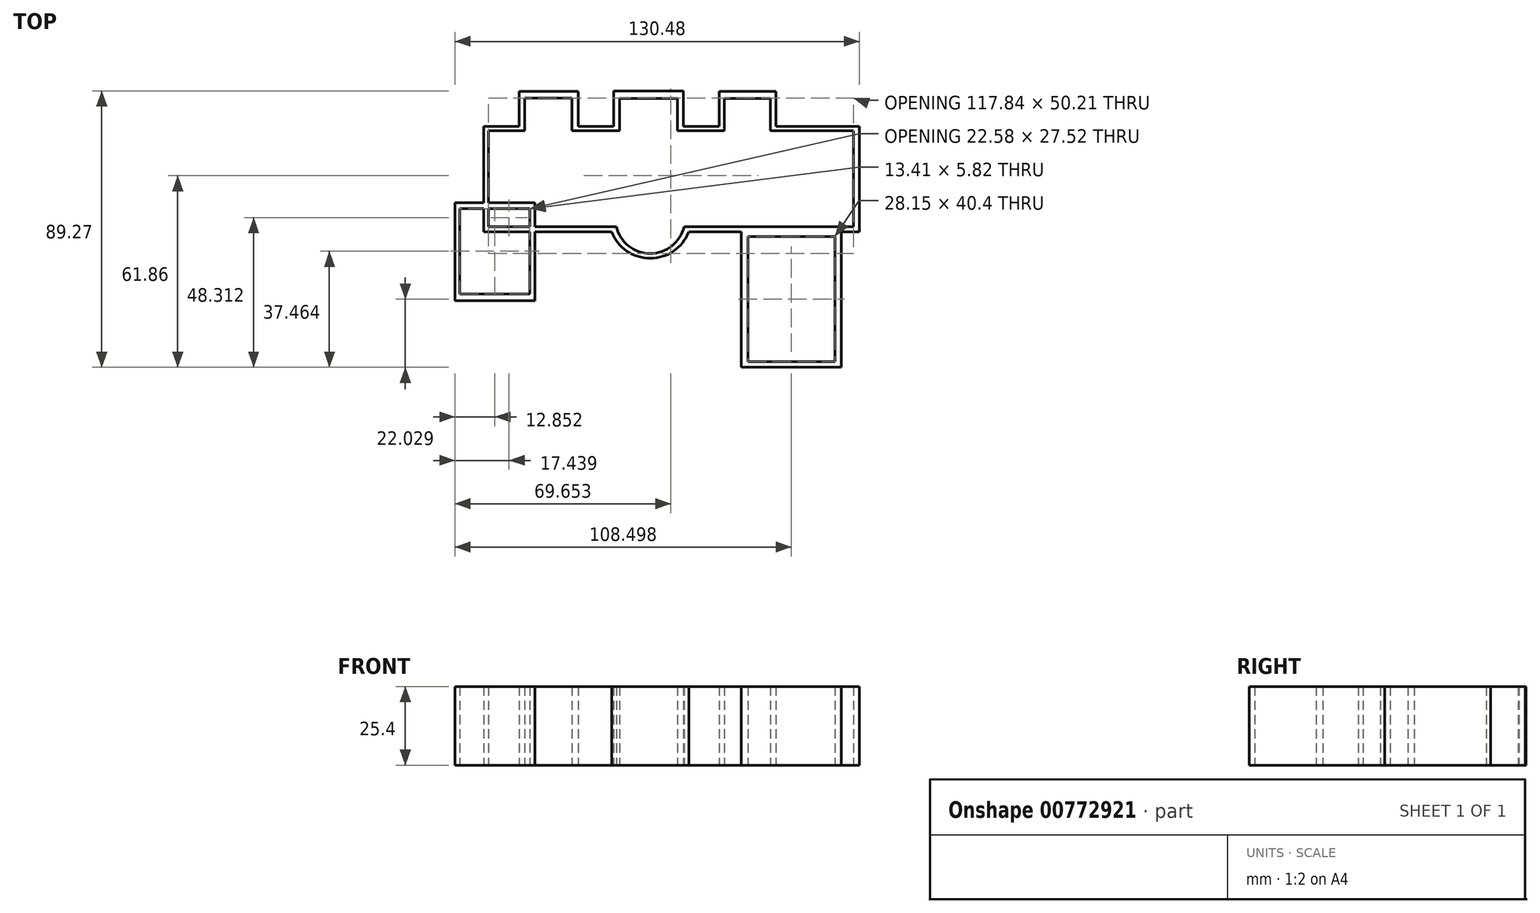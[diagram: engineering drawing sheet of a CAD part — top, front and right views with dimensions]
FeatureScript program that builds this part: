
annotation { "Feature Type Name" : "Feature", "Feature Type Description" : "" }
export const myFeature = defineFeature(function(context is Context, id is Id, definition is map)
    precondition{}
    {
        {
            var Q0;
            Q0=qCreatedBy(makeId("Top.planeOp"),FACE);
            var sketch = newSketch(context, id + "F0", { "sketchPlane" : qUnion([Q0])});
            skLineSegment(sketch, "E0.bottom", {"start": v(-53.74, 34.1) * mm, "end": v(67.5, 34.1) * mm});
            skLineSegment(sketch, "E0.top", {"start": v(-53.74, 0) * mm, "end": v(67.5, 0) * mm});
            skLineSegment(sketch, "E0.left", {"start": v(-53.74, 34.1) * mm, "end": v(-53.74, 0) * mm});
            skLineSegment(sketch, "E0.right", {"start": v(67.5, 34.1) * mm, "end": v(67.5, 0) * mm});
            skLineSegment(sketch, "E1.bottom", {"start": v(29.35, 0) * mm, "end": v(61.62, 0) * mm});
            skLineSegment(sketch, "E1.top", {"start": v(29.35, -43.74) * mm, "end": v(61.62, -43.74) * mm});
            skLineSegment(sketch, "E1.left", {"start": v(29.35, 0) * mm, "end": v(29.35, -43.74) * mm});
            skLineSegment(sketch, "E1.right", {"start": v(61.62, 0) * mm, "end": v(61.62, -43.74) * mm});
            skLineSegment(sketch, "E2.bottom", {"start": v(-62.98, 9.47) * mm, "end": v(-37.22, 9.47) * mm});
            skLineSegment(sketch, "E2.top", {"start": v(-62.98, -22.18) * mm, "end": v(-37.22, -22.18) * mm});
            skLineSegment(sketch, "E2.left", {"start": v(-62.98, 9.47) * mm, "end": v(-62.98, -22.18) * mm});
            skLineSegment(sketch, "E2.right", {"start": v(-37.22, 9.47) * mm, "end": v(-37.22, -22.18) * mm});
            skLineSegment(sketch, "E3.bottom", {"start": v(-42.26, 34.1) * mm, "end": v(-23.22, 34.1) * mm});
            skLineSegment(sketch, "E3.top", {"start": v(-42.26, 45.3) * mm, "end": v(-23.22, 45.3) * mm});
            skLineSegment(sketch, "E3.left", {"start": v(-42.26, 34.1) * mm, "end": v(-42.26, 45.3) * mm});
            skLineSegment(sketch, "E3.right", {"start": v(-23.22, 34.1) * mm, "end": v(-23.22, 45.3) * mm});
            skLineSegment(sketch, "E4.top", {"start": v(22.28, 45.3) * mm, "end": v(40.48, 45.3) * mm});
            skLineSegment(sketch, "E4.left", {"start": v(22.28, 34.1) * mm, "end": v(22.28, 45.3) * mm});
            skLineSegment(sketch, "E4.right", {"start": v(40.48, 34.1) * mm, "end": v(40.48, 45.3) * mm});
            skLineSegment(sketch, "E5.top", {"start": v(-11.74, 45.53) * mm, "end": v(10.63, 45.53) * mm});
            skLineSegment(sketch, "E5.left", {"start": v(-11.74, 34.1) * mm, "end": v(-11.74, 45.53) * mm});
            skLineSegment(sketch, "E5.right", {"start": v(10.63, 34.1) * mm, "end": v(10.63, 45.53) * mm});
            skLineSegment(sketch, "E6.bottom", {"start": v(-61.42, 7.48) * mm, "end": v(-38.84, 7.48) * mm});
            skLineSegment(sketch, "E6.top", {"start": v(-61.42, -20.04) * mm, "end": v(-38.84, -20.04) * mm});
            skLineSegment(sketch, "E6.left", {"start": v(-61.42, 7.48) * mm, "end": v(-61.42, -20.04) * mm});
            skLineSegment(sketch, "E6.right", {"start": v(-38.84, 7.48) * mm, "end": v(-38.84, -20.04) * mm});
            skLineSegment(sketch, "E7.bottom", {"start": v(-52.24, 32.7) * mm, "end": v(65.6, 32.7) * mm});
            skLineSegment(sketch, "E7.top", {"start": v(-52.24, 1.66) * mm, "end": v(65.6, 1.66) * mm});
            skLineSegment(sketch, "E7.left", {"start": v(-52.24, 32.7) * mm, "end": v(-52.24, 1.66) * mm});
            skLineSegment(sketch, "E7.right", {"start": v(65.6, 32.7) * mm, "end": v(65.6, 1.66) * mm});
            skLineSegment(sketch, "E8.bottom", {"start": v(31.44, -1.51) * mm, "end": v(59.6, -1.51) * mm});
            skLineSegment(sketch, "E8.top", {"start": v(31.44, -41.9) * mm, "end": v(59.6, -41.9) * mm});
            skLineSegment(sketch, "E8.left", {"start": v(31.44, -1.51) * mm, "end": v(31.44, -41.9) * mm});
            skLineSegment(sketch, "E8.right", {"start": v(59.6, -1.51) * mm, "end": v(59.6, -41.9) * mm});
            skLineSegment(sketch, "E9.bottom", {"start": v(-40.56, 43.23) * mm, "end": v(-25.23, 43.23) * mm});
            skLineSegment(sketch, "E9.top", {"start": v(-40.56, 34.1) * mm, "end": v(-25.23, 34.1) * mm});
            skLineSegment(sketch, "E9.left", {"start": v(-40.56, 43.23) * mm, "end": v(-40.56, 34.1) * mm});
            skLineSegment(sketch, "E9.right", {"start": v(-25.23, 43.23) * mm, "end": v(-25.23, 34.1) * mm});
            skLineSegment(sketch, "E10.bottom", {"start": v(-9.9, 43) * mm, "end": v(8.78, 43) * mm});
            skLineSegment(sketch, "E10.top", {"start": v(-9.9, 34.1) * mm, "end": v(8.78, 34.1) * mm});
            skLineSegment(sketch, "E10.left", {"start": v(-9.9, 43) * mm, "end": v(-9.9, 34.1) * mm});
            skLineSegment(sketch, "E10.right", {"start": v(8.78, 43) * mm, "end": v(8.78, 34.1) * mm});
            skLineSegment(sketch, "E11.bottom", {"start": v(23.9, 43) * mm, "end": v(38.76, 43) * mm});
            skLineSegment(sketch, "E11.top", {"start": v(23.9, 34.1) * mm, "end": v(38.76, 34.1) * mm});
            skLineSegment(sketch, "E11.left", {"start": v(23.9, 43) * mm, "end": v(23.9, 34.1) * mm});
            skLineSegment(sketch, "E11.right", {"start": v(38.76, 43) * mm, "end": v(38.76, 34.1) * mm});
            skArc(sketch, "E12", {"start": v(-12.45, 0) * mm, "mid": v(-0.02, -8.53) * mm, "end": v(12.4, 0) * mm});
            skArc(sketch, "E13", {"start": v(-10.96, 1.66) * mm, "mid": v(-0.02, -6.99) * mm, "end": v(10.91, 1.66) * mm});
            skLineSegment(sketch, "E14", {"start": v(31.44, -1.51) * mm, "end": v(31.44, 1.66) * mm});
            skLineSegment(sketch, "E15", {"start": v(-40.56, 34.1) * mm, "end": v(-40.56, 32.7) * mm});
            skLineSegment(sketch, "E16", {"start": v(-25.23, 34.1) * mm, "end": v(-25.23, 32.7) * mm});
            skLineSegment(sketch, "E17", {"start": v(-9.9, 34.1) * mm, "end": v(-9.9, 32.7) * mm});
            skLineSegment(sketch, "E18", {"start": v(8.78, 34.1) * mm, "end": v(8.78, 32.7) * mm});
            skLineSegment(sketch, "E19", {"start": v(23.9, 34.1) * mm, "end": v(23.9, 32.7) * mm});
            skLineSegment(sketch, "E20", {"start": v(38.76, 34.1) * mm, "end": v(38.76, 32.7) * mm});
            skSolve(sketch);
        }
        {
            var Q0;
            Q0=makeQuery(id+"F0.imprint","IMPRINT",FACE,{"disambiguationData":[TD([[makeQuery(id+"F0.imprint","IMPRINT",EDGE,{"derivedFrom":sQuery(id+"F0.wireOp",EDGE,"E5.top")}),-1.0]])]});
            var Q1;
            Q1=makeQuery(id+"F0.imprint","IMPRINT",FACE,{"disambiguationData":[TD([[makeQuery(id+"F0.imprint","IMPRINT",EDGE,{"derivedFrom":sQuery(id+"F0.wireOp",EDGE,"E3.top")}),-1.0]])]});
            var Q2;
            {var subQ0=sQuery(id+"F0.wireOp",EDGE,"E16");Q2=makeQuery(id+"F0.imprint","IMPRINT",FACE,{"disambiguationData":[TD([[makeQuery(id+"F0.imprint","IMPRINT",EDGE,{"derivedFrom":subQ0}),1.0]])]});}
            var Q3;
            {var subQ3=sQuery(id+"F0.wireOp",EDGE,"E15");Q3=makeQuery(id+"F0.imprint","IMPRINT",FACE,{"disambiguationData":[TD([[makeQuery(id+"F0.imprint","IMPRINT",EDGE,{"derivedFrom":subQ3}),-1.0]])]});}
            var Q4;
            {var subQ0=sQuery(id+"F0.wireOp",EDGE,"E2.top");Q4=makeQuery(id+"F0.imprint","IMPRINT",FACE,{"disambiguationData":[TD([[makeQuery(id+"F0.imprint","IMPRINT",EDGE,{"derivedFrom":subQ0}),1.0]])]});}
            var Q5;
            {var subQ1=sQuery(id+"F0.wireOp",EDGE,"E0.top");var subQ6=sQuery(id+"F0.wireOp",EDGE,"E0.left");var subQ11=makeQuery(id+"F0.imprint","INTERSECT",VERTEX,{"derivedFrom":[subQ1,subQ6]});Q5=makeQuery(id+"F0.imprint","IMPRINT",FACE,{"disambiguationData":[TD([[makeQuery(id+"F0.imprint","IMPRINT",EDGE,{"disambiguationData":[TD([[subQ11,-1.0]])],"derivedFrom":subQ1}),1.0]])]});}
            var Q6;
            {var subQ5=sQuery(id+"F0.wireOp",EDGE,"E2.right");var subQ6=sQuery(id+"F0.wireOp",EDGE,"E2.bottom");var subQ7=makeQuery(id+"F0.imprint","INTERSECT",VERTEX,{"derivedFrom":[subQ6,subQ5]});Q6=makeQuery(id+"F0.imprint","IMPRINT",FACE,{"disambiguationData":[TD([[makeQuery(id+"F0.imprint","IMPRINT",EDGE,{"disambiguationData":[TD([[subQ7,1.0]])],"derivedFrom":subQ6}),-1.0]])]});}
            var Q7;
            {var subQ0=sQuery(id+"F0.wireOp",EDGE,"E2.bottom");var subQ1=sQuery(id+"F0.wireOp",EDGE,"E0.left");var subQ2=makeQuery(id+"F0.imprint","INTERSECT",VERTEX,{"derivedFrom":[subQ1,subQ0]});Q7=makeQuery(id+"F0.imprint","IMPRINT",FACE,{"disambiguationData":[TD([[makeQuery(id+"F0.imprint","IMPRINT",EDGE,{"disambiguationData":[TD([[subQ2,-1.0]])],"derivedFrom":subQ1}),1.0]])]});}
            var Q8;
            {var subQ0=sQuery(id+"F0.wireOp",EDGE,"E2.right");var subQ1=sQuery(id+"F0.wireOp",EDGE,"E0.top");var subQ2=makeQuery(id+"F0.imprint","INTERSECT",VERTEX,{"derivedFrom":[subQ1,subQ0]});Q8=makeQuery(id+"F0.imprint","IMPRINT",FACE,{"disambiguationData":[TD([[makeQuery(id+"F0.imprint","IMPRINT",EDGE,{"disambiguationData":[TD([[subQ2,1.0]])],"derivedFrom":subQ1}),1.0]])]});}
            var Q9;
            {var subQ5=sQuery(id+"F0.wireOp",EDGE,"E0.top");var subQ8=makeQuery(id+"F0.imprint","INTERSECT",VERTEX,{"disambiguationData":[OD(0.0)],"derivedFrom":[subQ5,sQuery(id+"F0.wireOp",EDGE,"E12")]});Q9=makeQuery(id+"F0.imprint","IMPRINT",FACE,{"disambiguationData":[TD([[makeQuery(id+"F0.imprint","IMPRINT",EDGE,{"disambiguationData":[TD([[subQ8,1.0]])],"derivedFrom":subQ5}),1.0]])]});}
            var Q10;
            {var subQ1=sQuery(id+"F0.wireOp",EDGE,"E0.top");var subQ5=makeQuery(id+"F0.imprint","INTERSECT",VERTEX,{"disambiguationData":[OD(1.0)],"derivedFrom":[subQ1,sQuery(id+"F0.wireOp",EDGE,"E12")]});Q10=makeQuery(id+"F0.imprint","IMPRINT",FACE,{"disambiguationData":[TD([[makeQuery(id+"F0.imprint","IMPRINT",EDGE,{"disambiguationData":[TD([[subQ5,1.0]])],"derivedFrom":subQ1}),1.0]])]});}
            var Q11;
            {var subQ0=sQuery(id+"F0.wireOp",EDGE,"E12");Q11=makeQuery(id+"F0.imprint","IMPRINT",FACE,{"disambiguationData":[TD([[makeQuery(id+"F0.imprint","IMPRINT",EDGE,{"derivedFrom":subQ0}),1.0]])]});}
            var Q12;
            Q12=makeQuery(id+"F0.imprint","IMPRINT",FACE,{"disambiguationData":[TD([[makeQuery(id+"F0.imprint","IMPRINT",EDGE,{"derivedFrom":sQuery(id+"F0.wireOp",EDGE,"E1.top")}),1.0]])]});
            var Q13;
            {var subQ0=sQuery(id+"F0.wireOp",EDGE,"E0.right");Q13=makeQuery(id+"F0.imprint","IMPRINT",FACE,{"disambiguationData":[TD([[makeQuery(id+"F0.imprint","IMPRINT",EDGE,{"derivedFrom":subQ0}),-1.0]])]});}
            var Q14;
            Q14=makeQuery(id+"F0.imprint","IMPRINT",FACE,{"disambiguationData":[TD([[makeQuery(id+"F0.imprint","IMPRINT",EDGE,{"derivedFrom":sQuery(id+"F0.wireOp",EDGE,"E4.top")}),-1.0]])]});
            var Q15;
            {var subQ0=sQuery(id+"F0.wireOp",EDGE,"E18");Q15=makeQuery(id+"F0.imprint","IMPRINT",FACE,{"disambiguationData":[TD([[makeQuery(id+"F0.imprint","IMPRINT",EDGE,{"derivedFrom":subQ0}),1.0]])]});}
            extrude(context, id + "F1", {"entities" : qUnion([Q0, Q1, Q2, Q3, Q4, Q5, Q6, Q7, Q8, Q9, Q10, Q11, Q12, Q13, Q14, Q15]), "depth" : 25.4 * mm, "offsetDistance" : 25.4 * mm});
        }
    });
